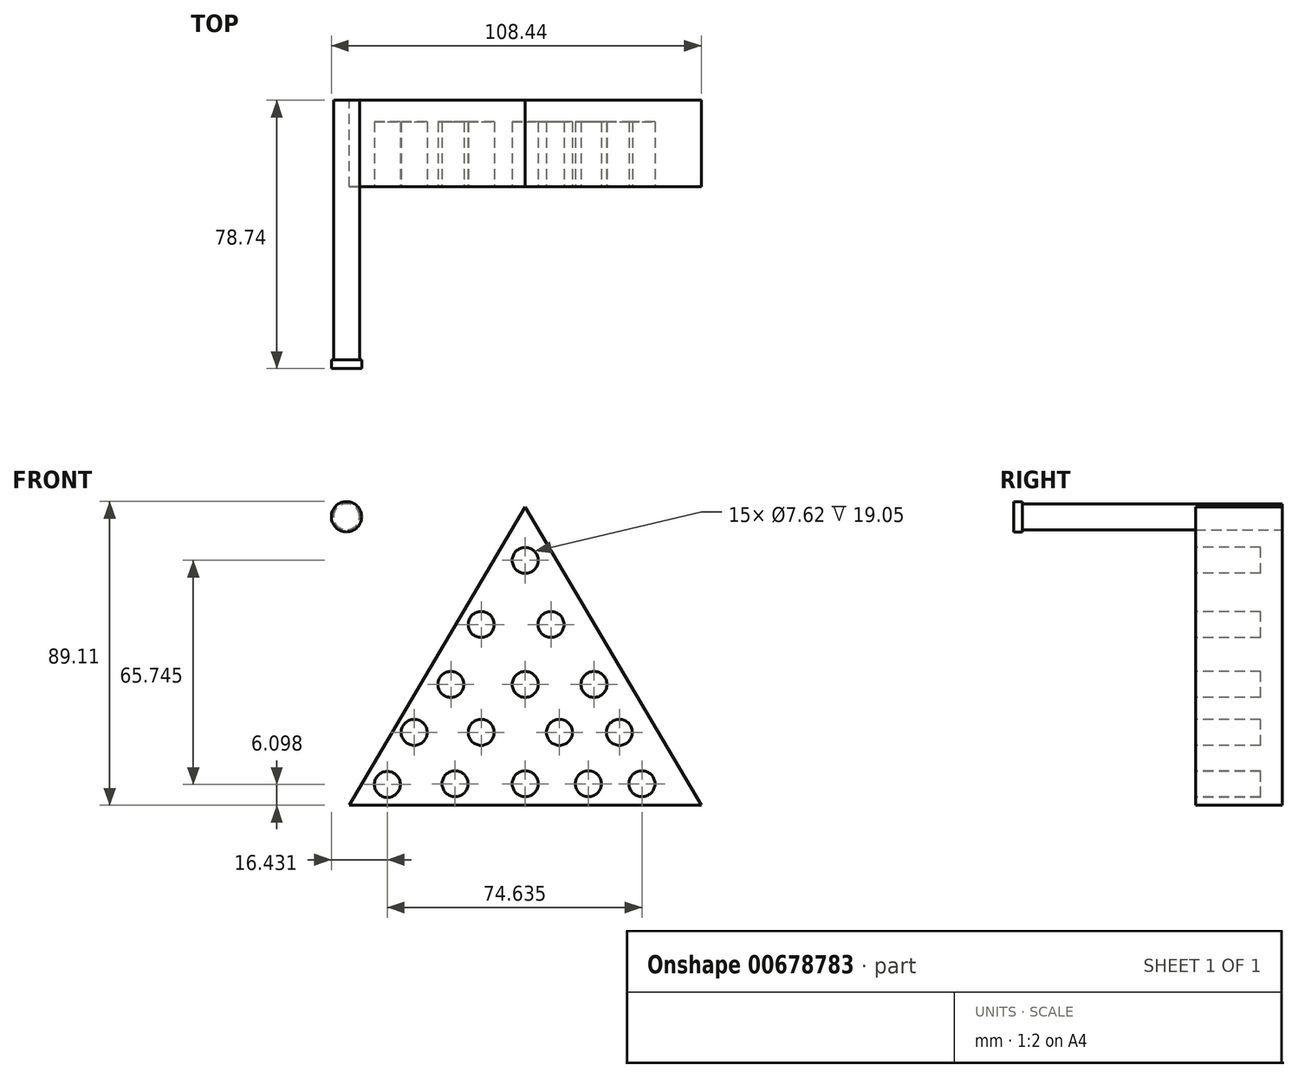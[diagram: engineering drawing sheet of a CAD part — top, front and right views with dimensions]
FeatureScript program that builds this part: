
annotation { "Feature Type Name" : "Feature", "Feature Type Description" : "" }
export const myFeature = defineFeature(function(context is Context, id is Id, definition is map)
    precondition{}
    {
        {
            var Q0;
            Q0=qCreatedBy(makeId("Front.planeOp"),FACE);
            var sketch = newSketch(context, id + "F0", { "sketchPlane" : qUnion([Q0])});
            skLineSegment(sketch, "E0", {"start": v(0, 49.52) * mm, "end": v(-51.54, -38.04) * mm});
            skLineSegment(sketch, "E1", {"start": v(0, 49.52) * mm, "end": v(51.6, -38.01) * mm});
            skLineSegment(sketch, "E2", {"start": v(-51.54, -38.04) * mm, "end": v(51.6, -38.01) * mm});
            skSolve(sketch);
        }
        {
            var Q0;
            Q0=makeQuery(id+"F0.imprint","IMPRINT",FACE,{"disambiguationData":[TD([[makeQuery(id+"F0.imprint","IMPRINT",EDGE,{"derivedFrom":sQuery(id+"F0.wireOp",EDGE,"E0")}),1.0]])]});
            extrude(context, id + "F1", {"entities" : qUnion([Q0]), "depth" : 25.4 * mm, "offsetDistance" : 25.4 * mm});
        }
        {
            var Q0;
            Q0=makeQuery(id+"F1.opExtrude","CAP_FACE",FACE,{"disambiguationData":[OSD([sQuery(id+"F0.wireOp",EDGE,"E0"),sQuery(id+"F0.wireOp",EDGE,"E1"),sQuery(id+"F0.wireOp",EDGE,"E2")])],"isStart":false});
            var sketch = newSketch(context, id + "F2", { "sketchPlane" : qUnion([Q0])});
            skCircle(sketch, "E3", {"center": v(0, 33.8) * mm, "radius": 3.81 * mm});
            skCircle(sketch, "E4", {"center": v(-12.92, 14.99) * mm, "radius": 3.81 * mm});
            skCircle(sketch, "E5", {"center": v(7.55, 14.99) * mm, "radius": 3.81 * mm});
            skCircle(sketch, "E6", {"center": v(-21.81, -2.58) * mm, "radius": 3.81 * mm});
            skCircle(sketch, "E7", {"center": v(0, -2.58) * mm, "radius": 3.81 * mm});
            skCircle(sketch, "E8", {"center": v(20.16, -2.58) * mm, "radius": 3.81 * mm});
            skCircle(sketch, "E9", {"center": v(-32.56, -16.64) * mm, "radius": 3.81 * mm});
            skCircle(sketch, "E10", {"center": v(-12.92, -16.64) * mm, "radius": 3.81 * mm});
            skCircle(sketch, "E11", {"center": v(10.03, -16.64) * mm, "radius": 3.81 * mm});
            skCircle(sketch, "E12", {"center": v(27.6, -16.64) * mm, "radius": 3.81 * mm});
            skCircle(sketch, "E13", {"center": v(-40.42, -31.94) * mm, "radius": 3.81 * mm});
            skCircle(sketch, "E14", {"center": v(-20.57, -31.74) * mm, "radius": 3.81 * mm});
            skCircle(sketch, "E15", {"center": v(0, -31.74) * mm, "radius": 3.81 * mm});
            skCircle(sketch, "E16", {"center": v(18.5, -31.74) * mm, "radius": 3.81 * mm});
            skCircle(sketch, "E17", {"center": v(34.22, -31.74) * mm, "radius": 3.81 * mm});
            skSolve(sketch);
        }
        {
            var Q0;
            Q0 = qSketchRegion(id + "F2", true);
            extrude(context, id + "F3", {"entities" : qUnion([Q0]), "operationType" : NewBodyOperationType.REMOVE, "oppositeDirection" : true, "depth" : 19.05 * mm, "offsetDistance" : 25.4 * mm});
        }
        {
            var Q0;
            Q0=qCreatedBy(makeId("Front.planeOp"),FACE);
            var sketch = newSketch(context, id + "F4", { "sketchPlane" : qUnion([Q0])});
            skCircle(sketch, "E18", {"center": v(-52.4, 46.62) * mm, "radius": 3.81 * mm});
            skSolve(sketch);
        }
        {
            var Q0;
            Q0 = qSketchRegion(id + "F4", true);
            extrude(context, id + "F5", {"entities" : qUnion([Q0]), "depth" : 76.2 * mm, "offsetDistance" : 25.4 * mm});
        }
        {
            var Q0;
            Q0=makeQuery(id+"F5.opExtrude","CAP_FACE",FACE,{"disambiguationData":[OSD([sQuery(id+"F4.wireOp",EDGE,"E18")])],"isStart":false});
            var sketch = newSketch(context, id + "F6", { "sketchPlane" : qUnion([Q0])});
            skCircle(sketch, "E19", {"center": v(-52.4, 46.62) * mm, "radius": 4.45 * mm});
            skSolve(sketch);
        }
        {
            var Q0;
            Q0 = qSketchRegion(id + "F6", true);
            extrude(context, id + "F7", {"entities" : qUnion([Q0]), "operationType" : NewBodyOperationType.ADD, "depth" : 2.54 * mm, "offsetDistance" : 25.4 * mm});
        }
    });
